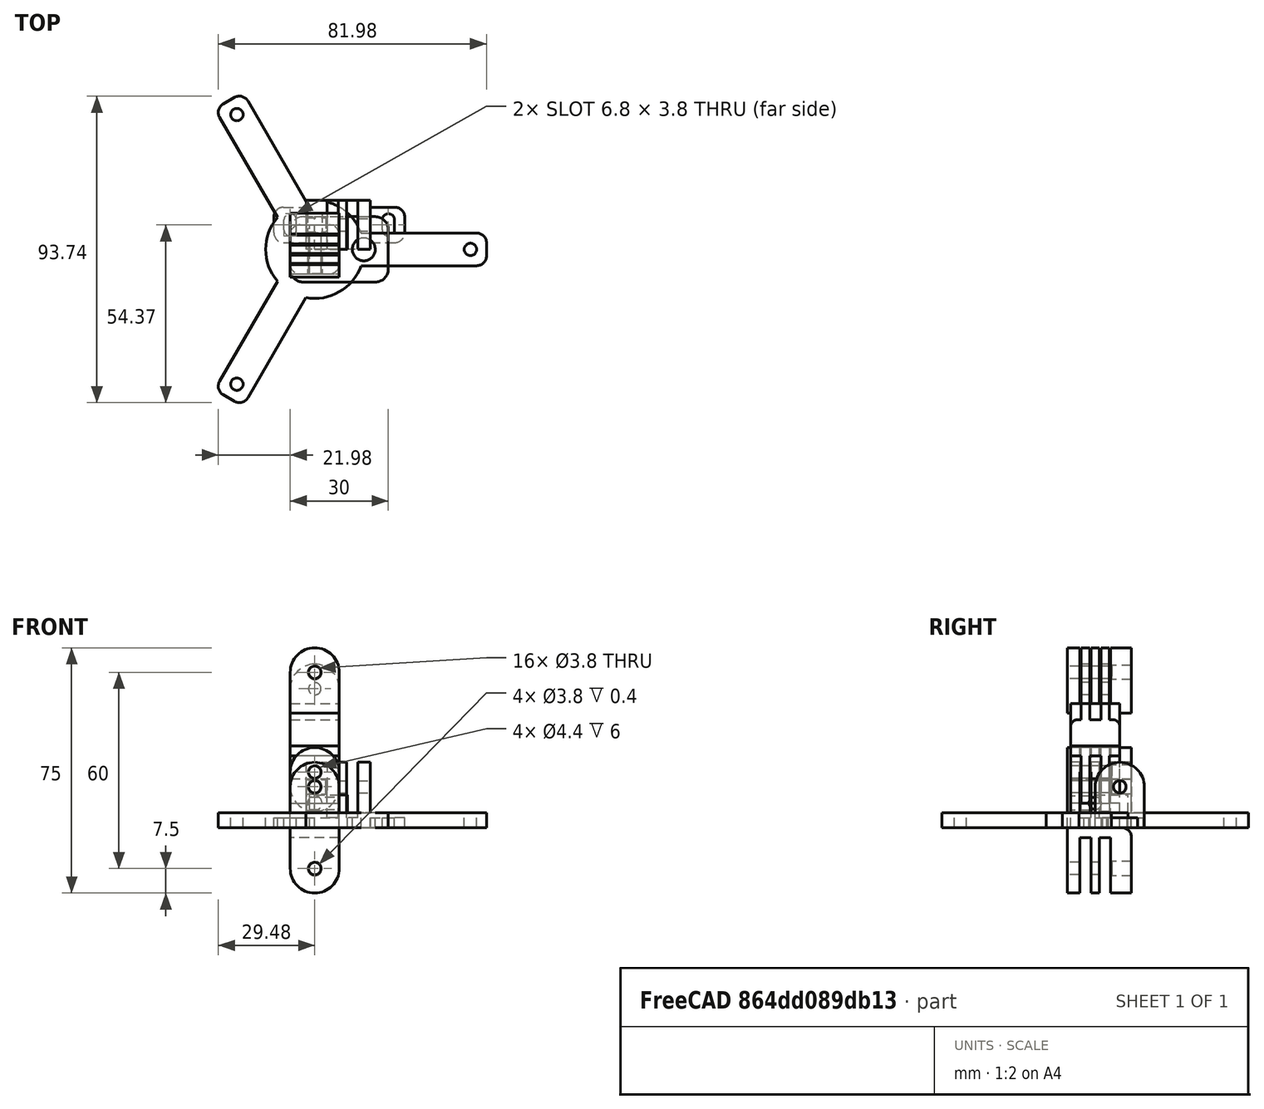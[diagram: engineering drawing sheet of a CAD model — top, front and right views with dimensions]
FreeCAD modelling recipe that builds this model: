
FCSTD DOCUMENT  (FreeCAD 0.20R29410 (Git))
Label: camera_stand
License: FreeArt
LicenseURL: http://artlibre.org/licence/lal
objects: Part::Box×12, Part::MultiFuse×11, Part::Cylinder×10, PartDesign::FeatureBase×9, PartDesign::Body×9, App::Part×8, Part::Cut×6, Part::Fillet×4, Part::FeaturePython×3, Spreadsheet::Sheet×1, Part::Feature×1
note: 65 computed .brp shape members not serialized (recipe doc carries the construction recipe); baked Part::Feature solids carry a one-line shape summary decoded from their .brp

FEATURE [Part::Box] Box  label="main stick"
  AttacherType = Attacher::AttachEngine3D
  Height = 10
  Length = 10
  Width = 10
FEATURE [Spreadsheet::Sheet] Spreadsheet  label="p"
  cells = A1=stick_width; B1(stick_width)=15; A2=stick_width_side_extra; B2(stick_width_side_extra)=1; A3=stick_width_insert_extra; B3(stick_width_insert_extra)=3.6; A4=side_extract_z; B4(side_extract_z)=17; A5=extract_y; B5(extract_y)=3; A6=extract_y_gap; B6(extract_y_gap)=0.4; A7=hole_r; B7(hole_r)=1.9; A8=insert_hole_r; B8(insert_hole_r)=2.2; A9=insert_z; B9(insert_z)=6; A10=cylinder_r; B10(cylinder_r)==stick_width / 2; A11=cylinder_extra_z; B11(cylinder_extra_z)=5; A13=part_length; B13(part_length)=20; A14=part_length30; B14(part_length30)=30; A16=stand_r; B16(stand_r)=15; A17=stand_stick_length; B17(stand_stick_length)=45; A18=stand_stick_width; B18(stand_stick_width)=10; A19=stand_z; B19(stand_z)=4.5; A21=zero_attach_length; B21(zero_attach_length)=30; A22=zero_attach_width; B22(zero_attach_width)=20; A23=zero_attach_z; B23(zero_attach_z)=4.5; A24=zero_bolt_hole_r; B24(zero_bolt_hole_r)=3.5
FEATURE [Part::Box] Box002  label="side cube"
  AttacherType = Attacher::AttachEngine3D
  Height = 12.5
  Length = 15
  Placement = pos=(-7.5,-8.5,0) rot=(0,0,1;0rad)
  Width = 19.6
  expr: .Placement.Base.x = -Spreadsheet.stick_width / 2
  expr: .Placement.Base.y = -<<p>>.stick_width / 2 - <<p>>.stick_width_side_extra
  expr: Height = <<p>>.cylinder_extra_z + <<p>>.cylinder_r
  expr: Length = <<p>>.stick_width
  expr: Width = <<p>>.stick_width + <<p>>.stick_width_side_extra + <<p>>.stick_width_insert_extra
FEATURE [Part::Cylinder] Cylinder  label="outer cylinder"
  Angle = 360
  AttacherType = Attacher::AttachEngine3D
  FirstAngle = 0
  Height = 19.6
  Placement = pos=(0,11.1,12.5) rot=(1,0,0;1.5708rad)
  Radius = 7.5
  SecondAngle = 0
  expr: .Placement.Base.y = <<p>>.stick_width / 2 + <<p>>.stick_width_insert_extra
  expr: .Placement.Base.z = <<p>>.cylinder_extra_z + <<p>>.cylinder_r
  expr: Height = <<p>>.stick_width + <<p>>.stick_width_side_extra + <<p>>.stick_width_insert_extra
  expr: Radius = <<p>>.cylinder_r
FEATURE [Part::MultiFuse] Fusion  label="side 3 fusion"
  Shapes = -> [Box002,Cylinder]
FEATURE [Part::Box] Box003  label="extract cube"
  AttacherType = Attacher::AttachEngine3D
  Height = 17
  Length = 15
  Placement = pos=(-7.5,-7.7,3) rot=(0,0,1;0rad)
  Width = 3.4
  expr: .Placement.Base.x = -<<p>>.stick_width / 2
  expr: .Placement.Base.y = -<<p>>.stick_width / 2 - <<p>>.extract_y_gap / 2
  expr: .Placement.Base.z = <<p>>.cylinder_extra_z + 2 * <<p>>.cylinder_r - Spreadsheet.side_extract_z
  expr: Height = <<p>>.side_extract_z
  expr: Length = <<p>>.stick_width
  expr: Width = <<p>>.extract_y + <<p>>.extract_y_gap
FEATURE [Part::FeaturePython] Array  label="side 3 extract cube array"  # Draft array (typed FeaturePython)
  Angle = 360
  ArrayType = 0
  Axis = (0,0,1)
  Base = -> Box003
  Center = (0,0,0)
  Fuse = false
  IntervalAxis = (0,0,0)
  IntervalX = (1,0,0)
  IntervalY = (0,6,0)
  IntervalZ = (0,0,1)
  NumberPolar = 1
  NumberX = 1
  NumberY = 2
  NumberZ = 1
  Placement = pos=(0,3,0) rot=(0,0,1;0rad)
  expr: .IntervalY.y = 2 * <<p>>.extract_y
  expr: .Placement.Base.y = (<<p>>.stick_width - 3 * <<p>>.extract_y) / 2
FEATURE [Part::Cylinder] Cylinder001  label="bolt hole"
  Angle = 360
  AttacherType = Attacher::AttachEngine3D
  FirstAngle = 0
  Height = 15
  Placement = pos=(0,0,6) rot=(0,0,1;0rad)
  Radius = 1.9
  SecondAngle = 0
  expr: .Placement.Base.z = <<p>>.insert_z
  expr: Height = <<p>>.stick_width
  expr: Radius = <<p>>.hole_r
FEATURE [Part::Cylinder] Cylinder002  label="insert hole"
  Angle = 360
  AttacherType = Attacher::AttachEngine3D
  FirstAngle = 0
  Height = 6
  Radius = 2.2
  SecondAngle = 0
  expr: Height = <<p>>.insert_z
  expr: Radius = <<p>>.insert_hole_r
FEATURE [Part::MultiFuse] Fusion001  label="hole fusion"
  Placement = pos=(0,11.1,12.5) rot=(1,0,0;1.5708rad)
  Shapes = -> [Cylinder001,Cylinder002]
  expr: .Placement.Base.y = <<p>>.stick_width / 2 + Spreadsheet.stick_width_insert_extra
  expr: .Placement.Base.z = <<p>>.cylinder_extra_z + <<p>>.cylinder_r
FEATURE [Part::MultiFuse] Fusion002  label="side 3 extract fusion"
  Shapes = -> [Fusion001,Array]
FEATURE [Part::Cut] Cut  label="side 3 cut"
  Base = -> Fusion
  Tool = -> Fusion002
FEATURE [App::Part] Part  label="side 3 part"
  Group = -> [Fusion,Cylinder002,Fusion001,Box002,Cylinder,Box003,Array,Cylinder001,Fusion002,Cut]
  Origin = -> Origin
FEATURE [Part::Box] Box004  label="side cube001"
  AttacherType = Attacher::AttachEngine3D
  Height = 12.5
  Length = 15
  Placement = pos=(-7.5,-7.5,0) rot=(0,0,1;0rad)
  Width = 15
  expr: .Placement.Base.x = -Spreadsheet.stick_width / 2
  expr: .Placement.Base.y = -<<p>>.stick_width / 2
  expr: Height = <<p>>.cylinder_extra_z + <<p>>.cylinder_r
  expr: Length = <<p>>.stick_width
  expr: Width = <<p>>.stick_width
FEATURE [Part::Cylinder] Cylinder003  label="outer cylinder001"
  Angle = 360
  AttacherType = Attacher::AttachEngine3D
  FirstAngle = 0
  Height = 15
  Placement = pos=(0,7.5,12.5) rot=(1,0,0;1.5708rad)
  Radius = 7.5
  SecondAngle = 0
  expr: .Placement.Base.y = <<p>>.stick_width / 2
  expr: .Placement.Base.z = <<p>>.cylinder_extra_z + <<p>>.cylinder_r
  expr: Height = <<p>>.stick_width
  expr: Radius = <<p>>.cylinder_r
FEATURE [Part::MultiFuse] Fusion003  label="side 2 fusion"
  Shapes = -> [Box004,Cylinder003]
FEATURE [Part::Cylinder] Cylinder004  label="side 2 bolt hole"
  Angle = 360
  AttacherType = Attacher::AttachEngine3D
  FirstAngle = 0
  Height = 15
  Placement = pos=(0,7.5,12.5) rot=(1,0,0;1.5708rad)
  Radius = 1.9
  SecondAngle = 0
  expr: .Placement.Base.y = <<p>>.stick_width / 2
  expr: .Placement.Base.z = <<p>>.cylinder_extra_z + <<p>>.cylinder_r
  expr: Height = <<p>>.stick_width
  expr: Radius = <<p>>.hole_r
FEATURE [Part::Box] Box005  label="extract cube001"
  AttacherType = Attacher::AttachEngine3D
  Height = 17
  Length = 15
  Placement = pos=(-7.5,-7.7,3) rot=(0,0,1;0rad)
  Width = 3.4
  expr: .Placement.Base.x = -<<p>>.stick_width / 2
  expr: .Placement.Base.y = -<<p>>.stick_width / 2 - <<p>>.extract_y_gap / 2
  expr: .Placement.Base.z = <<p>>.cylinder_extra_z + 2 * <<p>>.cylinder_r - Spreadsheet.side_extract_z
  expr: Height = Spreadsheet.side_extract_z
  expr: Length = <<p>>.stick_width
  expr: Width = <<p>>.extract_y + <<p>>.extract_y_gap
FEATURE [Part::FeaturePython] Array001  label="side 2 extract cube array"  # Draft array (typed FeaturePython)
  Angle = 360
  ArrayType = 0
  Axis = (0,0,1)
  Base = -> Box005
  Center = (0,0,0)
  Fuse = false
  IntervalAxis = (0,0,0)
  IntervalX = (1,0,0)
  IntervalY = (0,6,0)
  IntervalZ = (0,0,1)
  NumberPolar = 1
  NumberX = 1
  NumberY = 3
  NumberZ = 1
  expr: .IntervalY.y = 2 * <<p>>.extract_y
FEATURE [Part::MultiFuse] Fusion004  label="side 2 extract fusion"
  Shapes = -> [Array001,Cylinder004]
FEATURE [Part::Cut] Cut001  label="side 2 cut"
  Base = -> Fusion003
  Tool = -> Fusion004
FEATURE [App::Part] Part001  label="side 2 part"
  Group = -> [Fusion003,Box004,Cylinder003,Box005,Array001,Cylinder004,Fusion004,Cut001]
  Origin = -> Origin001
FEATURE [PartDesign::FeatureBase] Clone
  BaseFeature = -> Cut001
FEATURE [PartDesign::Body] Body  label="side 2 cut clone"
  BaseFeature = -> Cut001
  Group = -> [Clone]
  Origin = -> Origin002
  Placement = pos=(-3e-15,0,25) rot=(0,1,0;3.14159rad)
  Tip = -> Clone
FEATURE [PartDesign::FeatureBase] Clone001
  BaseFeature = -> Cut
FEATURE [PartDesign::Body] Body001  label="side 3 cut clone"
  BaseFeature = -> Cut
  Group = -> [Clone001]
  Origin = -> Origin003
  Tip = -> Clone001
FEATURE [Part::Box] Box006  label="cube one"
  AttacherType = Attacher::AttachEngine3D
  Height = 20
  Length = 15
  Placement = pos=(-7.5,-7.5,15) rot=(0,0,1;0rad)
  Width = 15
  expr: .Placement.Base.x = -<<p>>.stick_width / 2
  expr: .Placement.Base.y = -<<p>>.stick_width / 2
  expr: .Placement.Base.z = <<p>>.stick_width
  expr: Height = <<p>>.part_length
  expr: Length = <<p>>.stick_width
  expr: Width = <<p>>.stick_width
FEATURE [PartDesign::FeatureBase] Clone002
  BaseFeature = -> Cut
FEATURE [PartDesign::Body] Body002  label="side 3 cut clone001"
  BaseFeature = -> Cut
  Group = -> [Clone002]
  Origin = -> Origin005
  Placement = pos=(0,0,35) rot=(0,0,1;0rad)
  Tip = -> Clone002
  expr: .Placement.Base.z = <<p>>.stick_width + <<p>>.part_length
FEATURE [Part::Box] Box007  label="holed one cube"
  AttacherType = Attacher::AttachEngine3D
  Height = 15
  Length = 9
  Placement = pos=(-1.5,-7.5,0) rot=(0,0,1;0rad)
  Width = 15
  expr: .Placement.Base.x = -<<p>>.stick_width / 2 + <<p>>.insert_z
  expr: .Placement.Base.y = -<<p>>.stick_width / 2
  expr: Height = <<p>>.stick_width
  expr: Length = <<p>>.stick_width - <<p>>.insert_z
  expr: Width = <<p>>.stick_width
FEATURE [Part::Box] Box008  label="insert holed cube"
  AttacherType = Attacher::AttachEngine3D
  Height = 15
  Length = 15
  Placement = pos=(-7.5,-7.5,0) rot=(0,0,1;0rad)
  Width = 6
  expr: .Placement.Base.x = -<<p>>.stick_width / 2
  expr: .Placement.Base.y = -<<p>>.stick_width / 2
  expr: Height = <<p>>.stick_width
  expr: Length = <<p>>.stick_width
  expr: Width = <<p>>.insert_z
FEATURE [Part::Cylinder] Cylinder005  label="insert hole001"
  Angle = 360
  AttacherType = Attacher::AttachEngine3D
  FirstAngle = 0
  Height = 6
  Placement = pos=(0,-1.5,7.5) rot=(1,0,0;1.5708rad)
  Radius = 2.2
  SecondAngle = 0
  expr: .Placement.Base.y = <<p>>.insert_z - <<p>>.stick_width / 2
  expr: .Placement.Base.z = <<p>>.stick_width / 2
  expr: Height = <<p>>.insert_z
  expr: Radius = <<p>>.insert_hole_r
FEATURE [Part::Cylinder] Cylinder006  label="bolt hole001"
  Angle = 360
  AttacherType = Attacher::AttachEngine3D
  FirstAngle = 0
  Height = 15
  Placement = pos=(-7.5,0,7.5) rot=(0,1,0;1.5708rad)
  Radius = 1.9
  SecondAngle = 0
  expr: .Placement.Base.x = -<<p>>.stick_width / 2
  expr: .Placement.Base.z = <<p>>.stick_width / 2
  expr: Height = <<p>>.stick_width
  expr: Radius = <<p>>.hole_r
FEATURE [Part::Cut] Cut002  label="one cube with bolt hole"
  Base = -> Box007
  Tool = -> Cylinder006
FEATURE [Part::MultiFuse] Fusion005  label="side 3 one fusion"
  Shapes = -> [Box006,Body002,Cut002]
FEATURE [App::Part] Part002  label="side 3 rotate part"
  Group = -> [Body002,Box007,Cut002,Cylinder006,Box006,Fusion005]
  Origin = -> Origin004
FEATURE [Part::Box] Box009  label="cube one001"
  AttacherType = Attacher::AttachEngine3D
  Height = 20
  Length = 15
  Placement = pos=(-7.5,-7.5,15) rot=(0,0,1;0rad)
  Width = 15
  expr: .Placement.Base.x = -<<p>>.stick_width / 2
  expr: .Placement.Base.y = -<<p>>.stick_width / 2
  expr: .Placement.Base.z = <<p>>.stick_width
  expr: Height = <<p>>.part_length
  expr: Length = <<p>>.stick_width
  expr: Width = <<p>>.stick_width
FEATURE [PartDesign::FeatureBase] Clone004
  BaseFeature = -> Cut001
FEATURE [PartDesign::Body] Body004  label="side 2 cut clone001"
  BaseFeature = -> Cut001
  Group = -> [Clone004]
  Origin = -> Origin008
  Placement = pos=(0,0,35) rot=(0,0,1;0rad)
  Tip = -> Clone004
  expr: .Placement.Base.z = <<p>>.stick_width + <<p>>.part_length
FEATURE [Part::Cut] Cut004  label="one cube with insert hole cut"
  Base = -> Box008
  Tool = -> Cylinder005
FEATURE [Part::MultiFuse] Fusion006  label="side 2 one fusion00"
  Shapes = -> [Box009,Cut004,Body004]
FEATURE [App::Part] Part003  label="side 2 rotate part"
  Group = -> [Fusion006,Box009]
  Origin = -> Origin007
FEATURE [Part::Cylinder] Cylinder007  label="stand cylinder"
  Angle = 360
  AttacherType = Attacher::AttachEngine3D
  FirstAngle = 0
  Height = 4.5
  Radius = 15
  SecondAngle = 0
  expr: Height = <<p>>.stand_z
  expr: Radius = <<p>>.stand_r
FEATURE [Part::Box] Box010  label="stand stick"
  AttacherType = Attacher::AttachEngine3D
  Height = 4.5
  Length = 45
  Placement = pos=(7.5,-5,0) rot=(0,0,1;0rad)
  Width = 10
  expr: .Placement.Base.x = <<p>>.stand_r / 2
  expr: .Placement.Base.y = -<<p>>.stand_stick_width / 2
  expr: Height = <<p>>.stand_z
  expr: Length = <<p>>.stand_stick_length
  expr: Width = <<p>>.stand_stick_width
FEATURE [Part::Fillet] Fillet  label="stand stick fillet"
  Base = -> Box010
  Edges = 2 edges r=3: [Edge5,Edge7]
FEATURE [PartDesign::FeatureBase] Clone005
  BaseFeature = -> Cut
FEATURE [PartDesign::Body] Body005  label="side 3 cut clone002"
  BaseFeature = -> Cut
  Group = -> [Clone005]
  Origin = -> Origin010
  Placement = pos=(0,0,4.5) rot=(0,0,1;0rad)
  Tip = -> Clone005
  expr: .Placement.Base.z = <<p>>.stand_z
FEATURE [Part::Box] Box011  label="zero attach cube"
  AttacherType = Attacher::AttachEngine3D
  Height = 4.5
  Length = 30
  Placement = pos=(-7.5,-10,0) rot=(0,0,1;0rad)
  Width = 20
  expr: .Placement.Base.x = -<<p>>.stick_width / 2
  expr: .Placement.Base.y = -<<p>>.zero_attach_width / 2
  expr: Height = <<p>>.zero_attach_z
  expr: Length = <<p>>.zero_attach_length
  expr: Width = <<p>>.zero_attach_width
FEATURE [PartDesign::Body] Body006  label="side 2 cut clone002"
  Origin = -> Origin012
  Placement = pos=(0,0,4.5) rot=(0,0,1;0rad)
  expr: .Placement.Base.z = <<p>>.zero_attach_z
FEATURE [PartDesign::FeatureBase] Clone006
  BaseFeature = -> Cut001
FEATURE [Part::Cylinder] Cylinder008  label="zero attach hole"
  Angle = 360
  AttacherType = Attacher::AttachEngine3D
  FirstAngle = 0
  Height = 4.5
  Placement = pos=(15,0,0) rot=(0,0,1;0rad)
  Radius = 3.5
  SecondAngle = 0
  expr: .Placement.Base.x = <<p>>.zero_attach_length - <<p>>.stick_width
  expr: Height = <<p>>.zero_attach_z
  expr: Radius = <<p>>.zero_bolt_hole_r
FEATURE [Part::Fillet] Fillet001  label="zero attach fillet"
  Base = -> Box011
  Edges = 4 edges r=4: [Edge1,Edge3,Edge5,Edge7]
FEATURE [Part::Fillet] Fillet002  label="zero attach hole fillet"
  Base = -> Clone006
  Edges = 4 edges r=3: [Edge1,Edge11,Edge13,Edge42]
  Placement = pos=(0,0,4.5) rot=(0,0,1;0rad)
  expr: .Placement.Base.z = <<p>>.zero_attach_z
FEATURE [Part::MultiFuse] Fusion008  label="zero attach fusion"
  Shapes = -> [Fillet001,Fillet002]
FEATURE [Part::Cut] Cut005  label="zero attachment"
  Base = -> Fusion008
  Tool = -> Cylinder008
FEATURE [App::Part] Part005  label="rpi zero attachment part"
  Group = -> [Fusion008,Fillet002,Cylinder008,Fillet001,Clone006,Box011,Cut005,Body006]
  Origin = -> Origin011
FEATURE [Part::Cylinder] Cylinder009  label="bolt hole002"
  Angle = 360
  AttacherType = Attacher::AttachEngine3D
  FirstAngle = 0
  Height = 4.5
  Placement = pos=(47.6,0,0) rot=(0,0,1;0rad)
  Radius = 1.9
  SecondAngle = 0
  expr: .Placement.Base.x = <<p>>.stand_stick_length + <<p>>.stand_r / 2 - <<p>>.hole_r - 3
  expr: Height = <<p>>.stand_z
  expr: Radius = <<p>>.hole_r
FEATURE [Part::Cut] Cut006  label="stant stick cut"
  Base = -> Fillet
  Tool = -> Cylinder009
FEATURE [Part::FeaturePython] Array002  label="stand stick array"  # Draft array (typed FeaturePython)
  Angle = 360
  ArrayType = 1
  Axis = (0,0,1)
  Base = -> Cut006
  Center = (0,0,0)
  Fuse = false
  IntervalAxis = (0,0,0)
  IntervalX = (1,0,0)
  IntervalY = (0,1,0)
  IntervalZ = (0,0,1)
  NumberPolar = 3
  NumberX = 2
  NumberY = 2
  NumberZ = 1
FEATURE [Part::MultiFuse] Fusion007  label="stand fusion"
  Shapes = -> [Cylinder007,Array002,Body005]
FEATURE [App::Part] Part004  label="stand part"
  Group = -> [Cylinder007,Array002,Body005,Fusion007]
  Origin = -> Origin009
FEATURE [Part::Feature] Cut003001  label="attach plane x dir001"
  shape: bbox 40 x 10.8 x 3 mm, 18 faces (baked)
FEATURE [PartDesign::FeatureBase] Clone007
  BaseFeature = -> Cut
FEATURE [PartDesign::Body] Body007  label="side 3 clone"
  BaseFeature = -> Cut
  Group = -> [Clone007]
  Origin = -> Origin013
  Placement = pos=(8.5,7.5,0) rot=(0,0,1;1.5708rad)
  Tip = -> Clone007
  expr: .Placement.Base.x = <<p>>.stick_width / 2 + 1
  expr: .Placement.Base.y = <<p>>.stick_width / 2
FEATURE [Part::MultiFuse] Fusion009  label="hole board attachment fusion"
  Shapes = -> [Body007,Cut003001]
FEATURE [App::Part] Part006  label="hole board attachment part"
  Group = -> [Cut003001,Body007,Fusion009]
  Origin = -> Origin014
FEATURE [Part::Box] Box012  label="cube one002"
  AttacherType = Attacher::AttachEngine3D
  Height = 30
  Length = 15
  Placement = pos=(-7.5,-7.5,0) rot=(0,0,1;0rad)
  Width = 15
  expr: .Placement.Base.x = -<<p>>.stick_width / 2
  expr: .Placement.Base.y = -<<p>>.stick_width / 2
  expr: Height = <<p>>.part_length30
  expr: Length = <<p>>.stick_width
  expr: Width = <<p>>.stick_width
FEATURE [PartDesign::FeatureBase] Clone008
  BaseFeature = -> Cut001
FEATURE [PartDesign::Body] Body008  label="side 2 cut clone003"
  BaseFeature = -> Cut001
  Group = -> [Clone008]
  Origin = -> Origin016
  Placement = pos=(0,0,30) rot=(0,0,1;0rad)
  Tip = -> Clone008
  expr: .Placement.Base.z = <<p>>.part_length30
FEATURE [PartDesign::FeatureBase] Clone009
  BaseFeature = -> Cut
FEATURE [PartDesign::Body] Body009  label="side 3 cut clone003"
  BaseFeature = -> Cut
  Group = -> [Clone009]
  Origin = -> Origin017
  Placement = pos=(0,0,0) rot=(0,1,0;3.14159rad)
  Tip = -> Clone009
FEATURE [Part::MultiFuse] Fusion010  label="extender stick fusion"
  Shapes = -> [Box012,Body008,Body009]
FEATURE [Part::Fillet] Fillet003  label="extender stick fillet"
  Base = -> Fusion010
  Edges = 4 edges: [Edge36 r=0.5,Edge40 r=2,Edge65 r=2,Edge69 r=3]
FEATURE [App::Part] Part007  label="extender stick"
  Group = -> [Box012,Body008,Fusion010,Body009,Fillet003]
  Origin = -> Origin015
